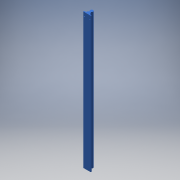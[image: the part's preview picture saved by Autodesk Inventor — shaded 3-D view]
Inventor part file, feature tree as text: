
AUTODESK INVENTOR PART (.ipt)
format: ipt  version: 2018 (Build 220112000, 112)  size: 142,336 bytes
history: native  units: mm
features: sketch x2, other x1, extrude x1, hole x1
ambient origin geometry x8: Origin, YZ Plane, XZ Plane, XY Plane, X Axis, Y Axis, Z Axis, Center Point
bodies: Body1 (feature_tree)
feature tree (5):
  other  "Sólido1"
  extrude  "Extrusão1"  Depth=25.0mm
  hole  "Furo1"  [1 undecoded]
  sketch  "Esboço1"  dims[d6=16.0mm d7=25.0mm]
  sketch  "Esboço3"  dims[d8=18.5mm d9=11.7mm d10=8.0mm d11=30.0deg d12=30.0deg d13=5.0mm d14=40.0mm d15=725.0mm d16=0.0mm d18=15.0mm d19=15.0mm d20=5.5mm d21=5.5mm d22=20.0mm d28=5.5mm d29=6.0mm d30=4.0mm d31=2.0mm d32=90.0deg d33=8.0mm d34=20.594885mm]
note: 1 required parameter value undecoded (feature->parameter linkage not recoverable at this tier; creation-order binding heuristic only, values carry confidence <= 0.55)
